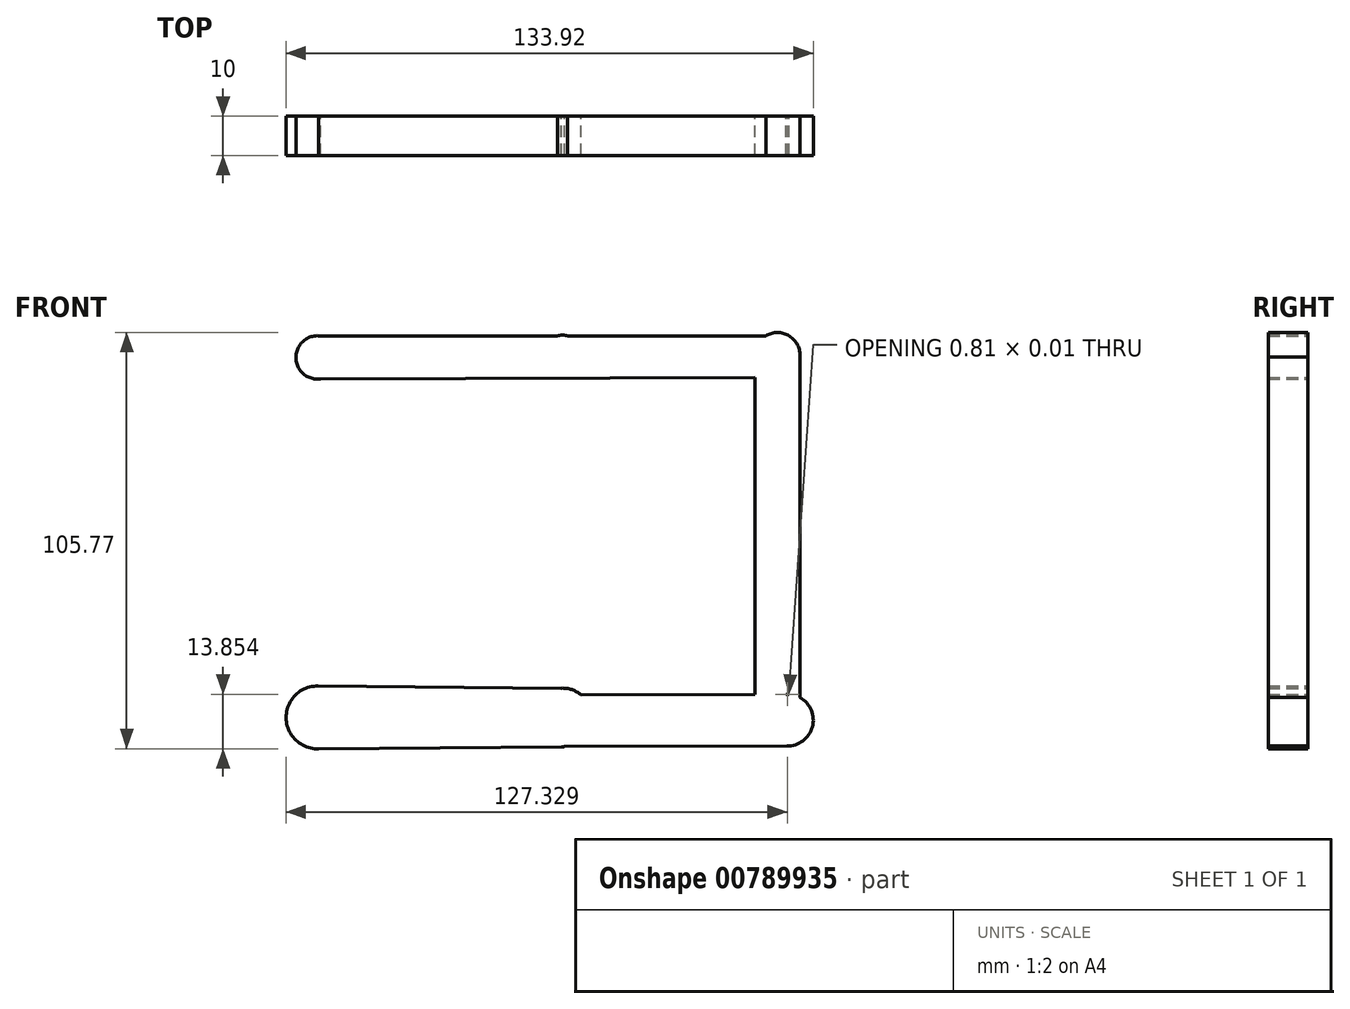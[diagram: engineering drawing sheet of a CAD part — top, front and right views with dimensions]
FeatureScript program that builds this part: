
annotation { "Feature Type Name" : "Feature", "Feature Type Description" : "" }
export const myFeature = defineFeature(function(context is Context, id is Id, definition is map)
    precondition{}
    {
        {
            var Q0;
            Q0=qCreatedBy(makeId("Front.planeOp"),FACE);
            var sketch = newSketch(context, id + "F0", { "sketchPlane" : qUnion([Q0])});
            skCircle(sketch, "E0", {"center": v(-41.53, 43.73) * mm, "radius": 5.5 * mm});
            skLineSegment(sketch, "E1", {"start": v(-41.8, 49.23) * mm, "end": v(20.04, 49.23) * mm});
            skLineSegment(sketch, "E2", {"start": v(-42.2, 38.27) * mm, "end": v(20.32, 38.44) * mm});
            skCircle(sketch, "E3", {"center": v(20.71, 43.92) * mm, "radius": 5.48 * mm});
            skLineSegment(sketch, "E4", {"start": v(20.04, 49.23) * mm, "end": v(74.31, 49.23) * mm});
            skLineSegment(sketch, "E5", {"start": v(20.32, 38.44) * mm, "end": v(74.59, 38.59) * mm});
            skCircle(sketch, "E6", {"center": v(75.31, 44.3) * mm, "radius": 5.76 * mm});
            skLineSegment(sketch, "E7", {"start": v(69.56, 44.3) * mm, "end": v(69.56, -48.42) * mm});
            skLineSegment(sketch, "E8", {"start": v(81.05, 44.76) * mm, "end": v(81.05, -47.64) * mm});
            skCircle(sketch, "E9", {"center": v(77.84, -48.42) * mm, "radius": 6.57 * mm});
            skLineSegment(sketch, "E10", {"start": v(78.22, -41.86) * mm, "end": v(21.2, -42.02) * mm});
            skLineSegment(sketch, "E11", {"start": v(78.03, -55) * mm, "end": v(21.17, -55.15) * mm});
            skCircle(sketch, "E12", {"center": v(20.72, -47.73) * mm, "radius": 7.44 * mm});
            skCircle(sketch, "E13", {"center": v(-41.53, -47.73) * mm, "radius": 7.98 * mm});
            skLineSegment(sketch, "E14", {"start": v(-41.53, -39.75) * mm, "end": v(21.2, -40.3) * mm});
            skLineSegment(sketch, "E15", {"start": v(-41.68, -55.7) * mm, "end": v(-35.77, -53.26) * mm});
            skLineSegment(sketch, "E16", {"start": v(-41.68, -55.7) * mm, "end": v(21.17, -55.15) * mm});
            skSolve(sketch);
        }
        {
            var Q0;
            Q0 = qSketchRegion(id + "F0", true);
            extrude(context, id + "F1", {"entities" : qUnion([Q0]), "depth" : 10 * mm, "offsetDistance" : 25 * mm});
        }
    });
